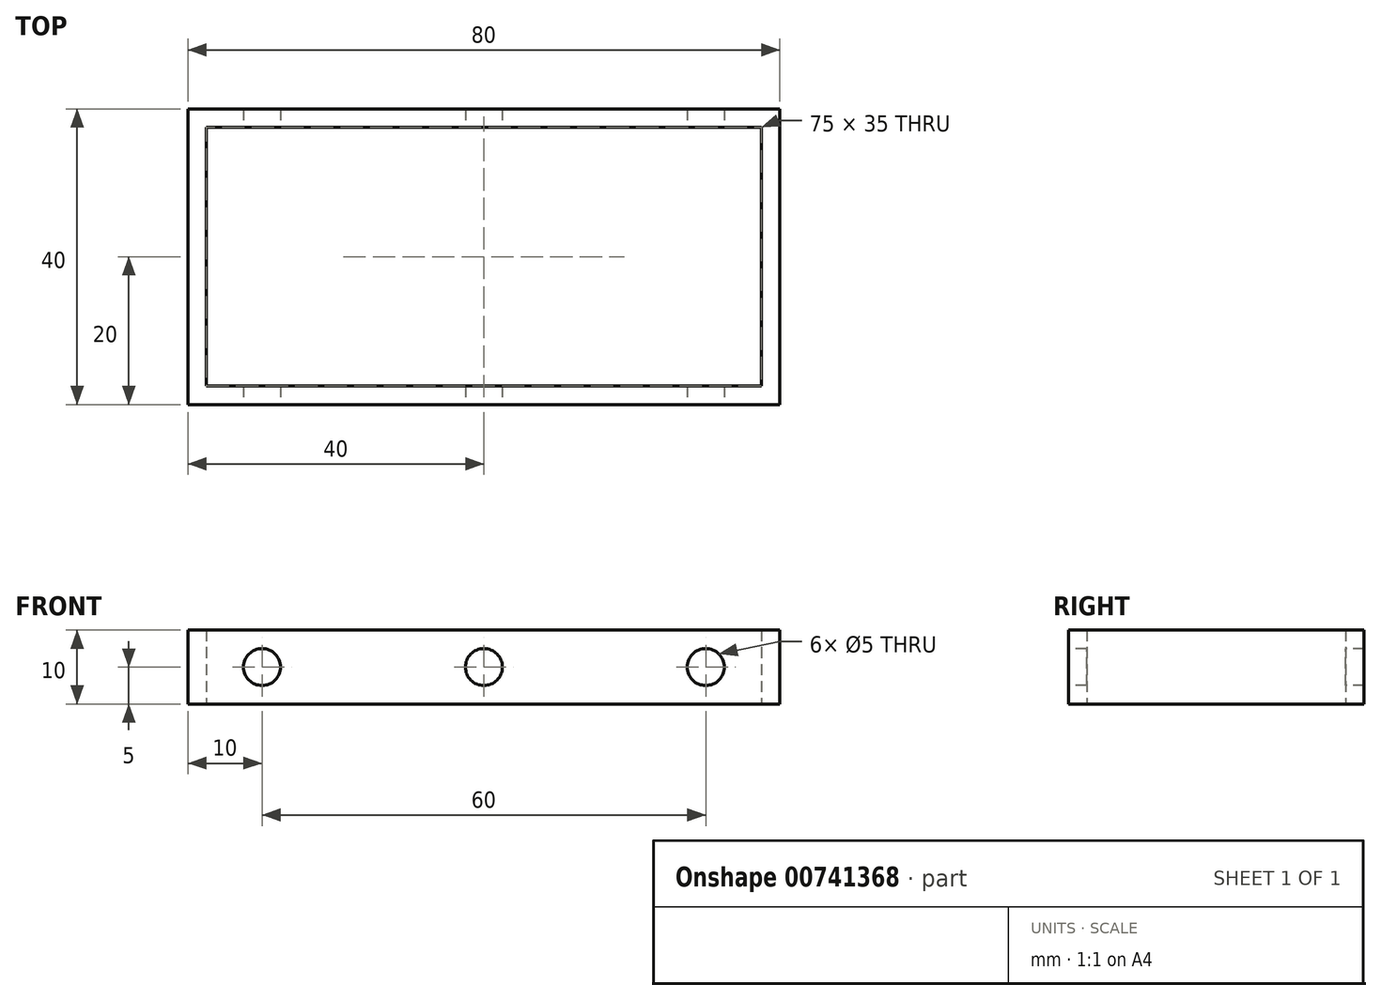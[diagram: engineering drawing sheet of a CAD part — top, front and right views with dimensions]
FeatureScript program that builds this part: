
annotation { "Feature Type Name" : "Feature", "Feature Type Description" : "" }
export const myFeature = defineFeature(function(context is Context, id is Id, definition is map)
    precondition{}
    {
        {
            var Q0;
            Q0=qCreatedBy(makeId("Top.planeOp"),FACE);
            var sketch = newSketch(context, id + "F0", { "sketchPlane" : qUnion([Q0])});
            skLineSegment(sketch, "E0.bottom", {"start": v(40, -20) * mm, "end": v(-40, -20) * mm});
            skLineSegment(sketch, "E0.top", {"start": v(40, 20) * mm, "end": v(-40, 20) * mm});
            skLineSegment(sketch, "E0.left", {"start": v(40, -20) * mm, "end": v(40, 20) * mm});
            skLineSegment(sketch, "E0.right", {"start": v(-40, -20) * mm, "end": v(-40, 20) * mm});
            skPoint(sketch, "E0.middle", {"position": v(0, 0) * mm});
            skLineSegment(sketch, "E1.0", {"start": v(37.5, 17.5) * mm, "end": v(-37.5, 17.5) * mm});
            skLineSegment(sketch, "E1.1", {"start": v(37.5, -17.5) * mm, "end": v(37.5, 17.5) * mm});
            skLineSegment(sketch, "E1.2", {"start": v(37.5, -17.5) * mm, "end": v(-37.5, -17.5) * mm});
            skLineSegment(sketch, "E1.3", {"start": v(-37.5, -17.5) * mm, "end": v(-37.5, 17.5) * mm});
            skSolve(sketch);
        }
        {
            var Q0;
            Q0 = qSketchRegion(id + "F0", true);
            extrude(context, id + "F1", {"entities" : qUnion([Q0]), "depth" : 10 * mm, "offsetDistance" : 25 * mm});
        }
        {
            var Q0;
            Q0=makeQuery(id+"F1.opExtrude","SWEPT_FACE",FACE,{"disambiguationData":[OSD([sQuery(id+"F0.wireOp",EDGE,"E0.bottom")])]});
            var sketch = newSketch(context, id + "F2", { "sketchPlane" : qUnion([Q0])});
            skLineSegment(sketch, "E2", {"start": v(-30, 5) * mm, "end": v(30, 5) * mm, "construction": true});
            skCircle(sketch, "E3", {"center": v(30, 5) * mm, "radius": 2.5 * mm});
            skCircle(sketch, "E4", {"center": v(-30, 5) * mm, "radius": 2.5 * mm});
            skCircle(sketch, "E5", {"center": v(0, 5) * mm, "radius": 2.5 * mm});
            skSolve(sketch);
        }
        {
            var Q0;
            Q0=makeQuery(id+"F2.imprint","IMPRINT",FACE,{"disambiguationData":[TD([[makeQuery(id+"F2.imprint","IMPRINT",EDGE,{"derivedFrom":sQuery(id+"F2.wireOp",EDGE,"E4")}),1.0]])]});
            var Q1;
            Q1=makeQuery(id+"F2.imprint","IMPRINT",FACE,{"disambiguationData":[TD([[makeQuery(id+"F2.imprint","IMPRINT",EDGE,{"derivedFrom":sQuery(id+"F2.wireOp",EDGE,"E5")}),1.0]])]});
            var Q2;
            Q2=makeQuery(id+"F2.imprint","IMPRINT",FACE,{"disambiguationData":[TD([[makeQuery(id+"F2.imprint","IMPRINT",EDGE,{"derivedFrom":sQuery(id+"F2.wireOp",EDGE,"E3")}),1.0]])]});
            extrude(context, id + "F3", {"entities" : qUnion([Q0, Q1, Q2]), "operationType" : NewBodyOperationType.REMOVE, "oppositeDirection" : true, "depth" : 47.9 * mm, "offsetDistance" : 25 * mm});
        }
    });
